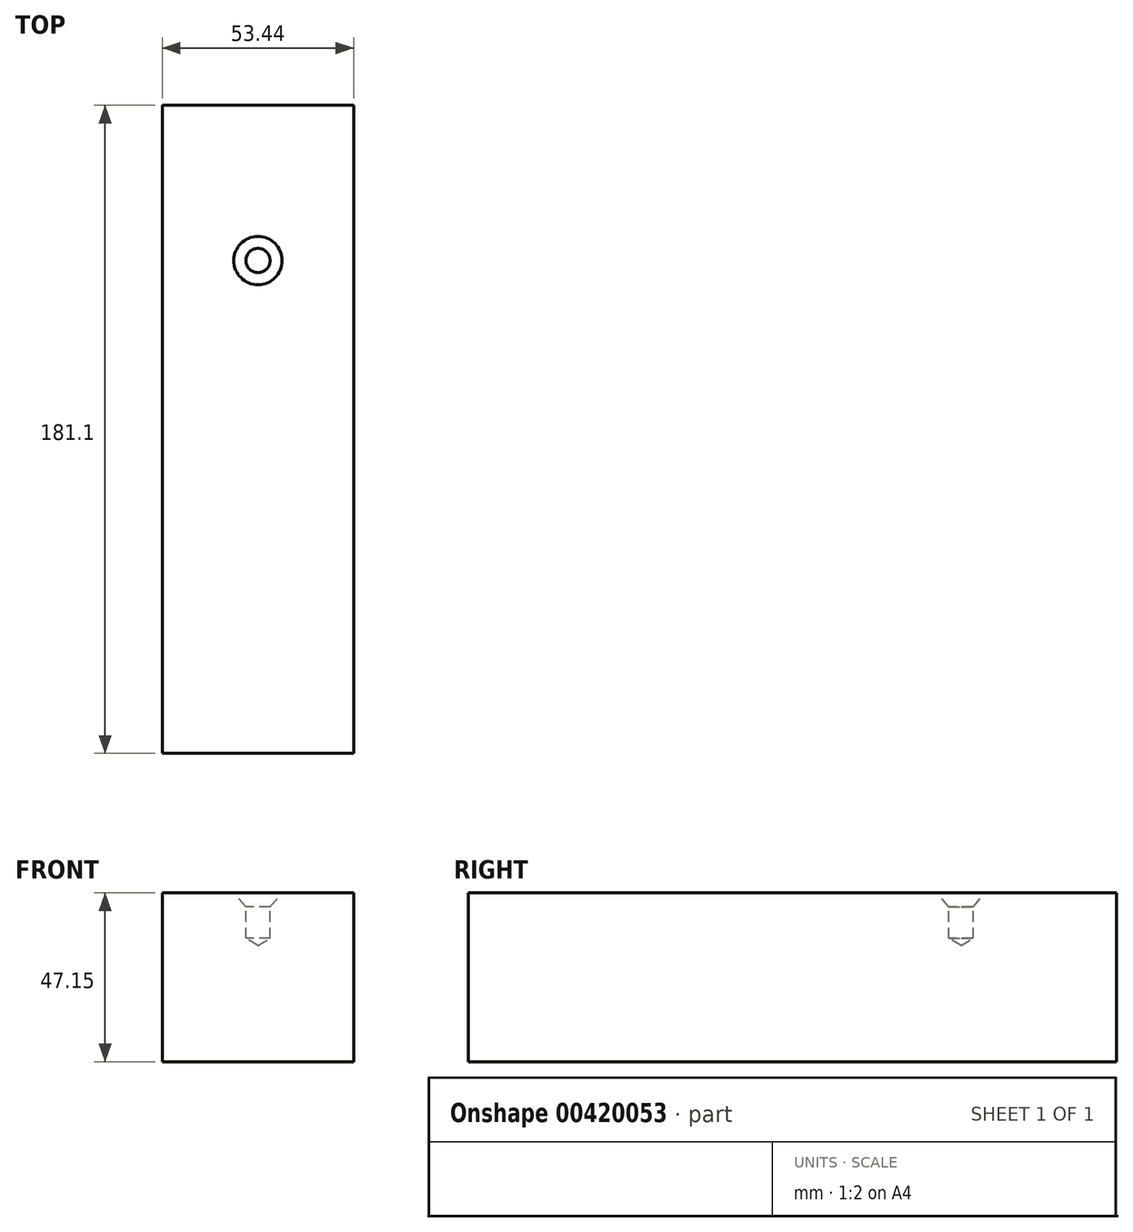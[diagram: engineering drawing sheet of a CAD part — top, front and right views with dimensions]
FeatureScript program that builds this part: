
annotation { "Feature Type Name" : "Feature", "Feature Type Description" : "" }
export const myFeature = defineFeature(function(context is Context, id is Id, definition is map)
    precondition{}
    {
        {
            var Q0;
            Q0=qCreatedBy(makeId("Front.planeOp"),FACE);
            var sketch = newSketch(context, id + "F0", { "sketchPlane" : qUnion([Q0])});
            skLineSegment(sketch, "E0", {"start": v(0, 0) * mm, "end": v(0, 47.15) * mm});
            skLineSegment(sketch, "E1", {"start": v(-1.8, 47.15) * mm, "end": v(53.44, 47.15) * mm});
            skLineSegment(sketch, "E2", {"start": v(53.44, 47.15) * mm, "end": v(53.44, 0) * mm});
            skLineSegment(sketch, "E3", {"start": v(53.44, 0) * mm, "end": v(0, 0) * mm});
            skSolve(sketch);
        }
        {
            var Q0;
            Q0 = qSketchRegion(id + "F0", true);
            extrude(context, id + "F1", {"entities" : qUnion([Q0]), "oppositeDirection" : true, "depth" : 181.1 * mm});
        }
        {
            var Q0;
            Q0=makeQuery(id+"F1.opExtrude","SWEPT_FACE",FACE,{"disambiguationData":[OSD([sQuery(id+"F0.wireOp",EDGE,"E1")])]});
            var sketch = newSketch(context, id + "F2", { "sketchPlane" : qUnion([Q0])});
            skCircle(sketch, "E4", {"center": v(26.72, 137.71) * mm, "radius": 11.44 * mm});
            skPoint(sketch, "E4.centerSnap0", {"position": v(26.72, 181.1) * mm});
            skSolve(sketch);
        }
        {
            var Q0;
            Q0=sQuery(id+"F2.wireOp",VERTEX,"E4.center");
            var Q1;
            Q1=makeQuery(id+"F1.opExtrude","SWEPT_BODY",BODY,{"disambiguationData":[OSD([sQuery(id+"F0.wireOp",EDGE,"E0"),sQuery(id+"F0.wireOp",EDGE,"E1"),sQuery(id+"F0.wireOp",EDGE,"E2"),sQuery(id+"F0.wireOp",EDGE,"E3")])]});
            hole(context, id + "F3", {"style" : HoleStyle.C_SINK, "endStyle" : HoleEndStyle.BLIND, "standardTappedOrClearance" : lookupTablePath({ "standard" : "ANSI", "fit" : "Normal (ASME)", "size" : "1/4", "type" : "Clearance" }), "standardBlindInLast" : lookupTablePath({ "fit" : "Free", "standard" : "ANSI", "size" : "1/4", "type" : "Clearance" }), "holeDiameter" : 6.76 * mm, "cSinkDiameter" : 13.5 * mm, "cSinkAngle" : 82 * degree, "holeDepth" : 12.7 * mm, "isTappedThrough" : true, "tappedDepth" : 12.7 * mm, "tapClearance" : 3, "locations" : qUnion([Q0]), "scope" : qUnion([Q1])});
        }
    });
